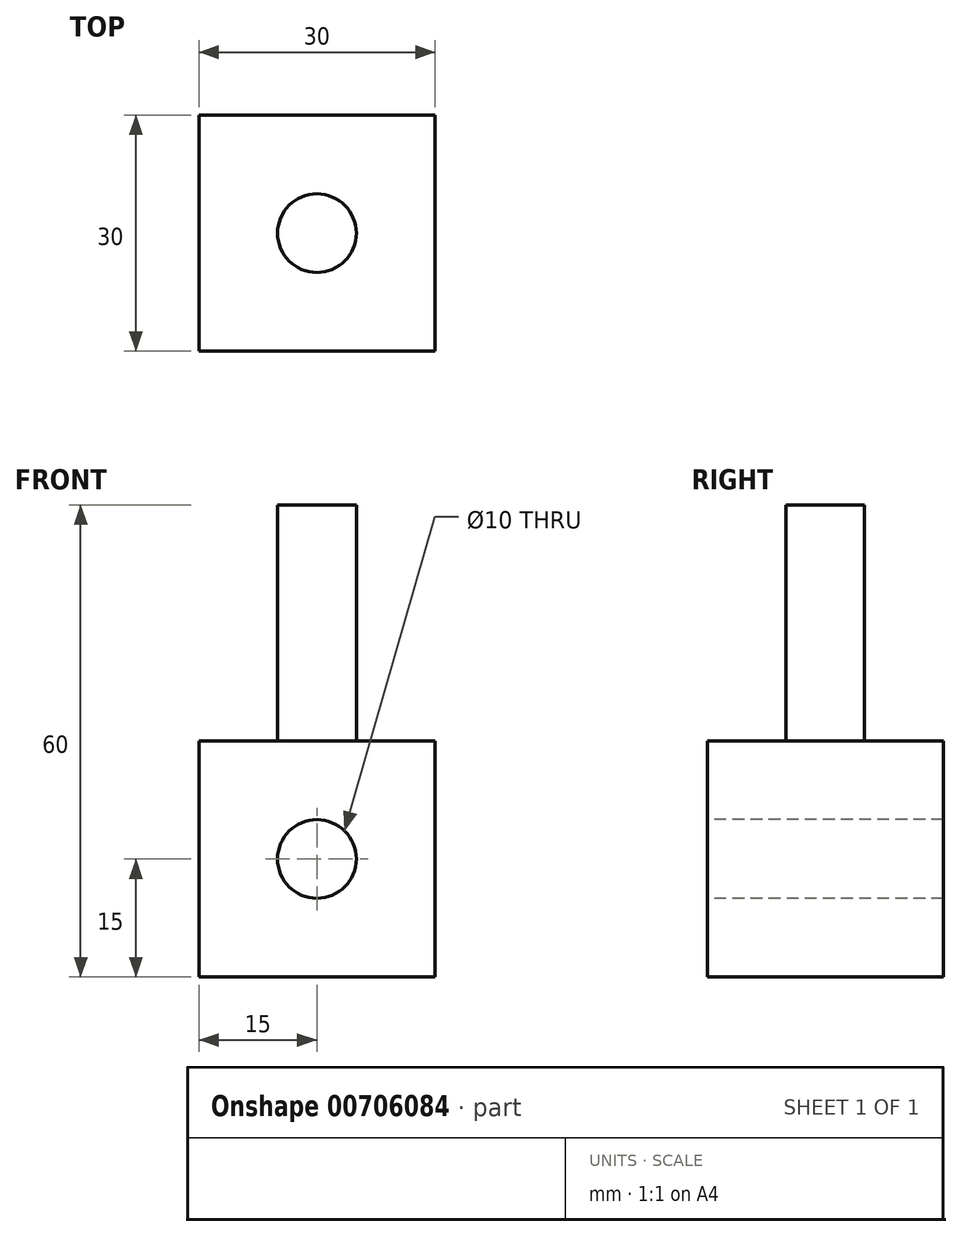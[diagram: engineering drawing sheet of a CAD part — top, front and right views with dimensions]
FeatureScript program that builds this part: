
annotation { "Feature Type Name" : "Feature", "Feature Type Description" : "" }
export const myFeature = defineFeature(function(context is Context, id is Id, definition is map)
    precondition{}
    {
        {
            var Q0;
            Q0=qCreatedBy(makeId("Front.planeOp"),FACE);
            var sketch = newSketch(context, id + "F0", { "sketchPlane" : qUnion([Q0])});
            skLineSegment(sketch, "E0.bottom", {"start": v(15, 15) * mm, "end": v(-15, 15) * mm});
            skLineSegment(sketch, "E0.top", {"start": v(15, -15) * mm, "end": v(-15, -15) * mm});
            skLineSegment(sketch, "E0.left", {"start": v(15, 15) * mm, "end": v(15, -15) * mm});
            skLineSegment(sketch, "E0.right", {"start": v(-15, 15) * mm, "end": v(-15, -15) * mm});
            skPoint(sketch, "E0.middle", {"position": v(0, 0) * mm});
            skSolve(sketch);
        }
        {
            var Q0;
            Q0 = qSketchRegion(id + "F0", true);
            extrude(context, id + "F1", {"entities" : qUnion([Q0]), "depth" : 30 * mm, "offsetDistance" : 25 * mm});
        }
        {
            var Q0;
            Q0=makeQuery(id+"F1.opExtrude","CAP_FACE",FACE,{"disambiguationData":[OSD([sQuery(id+"F0.wireOp",EDGE,"E0.bottom"),sQuery(id+"F0.wireOp",EDGE,"E0.top"),sQuery(id+"F0.wireOp",EDGE,"E0.left"),sQuery(id+"F0.wireOp",EDGE,"E0.right")])],"isStart":false});
            var sketch = newSketch(context, id + "F2", { "sketchPlane" : qUnion([Q0])});
            skCircle(sketch, "E1", {"center": v(0, 0) * mm, "radius": 5 * mm});
            skSolve(sketch);
        }
        {
            var Q0;
            Q0=makeQuery(id+"F2.imprint","IMPRINT",FACE,{"disambiguationData":[TD([[makeQuery(id+"F2.imprint","IMPRINT",EDGE,{"derivedFrom":sQuery(id+"F2.wireOp",EDGE,"E1")}),1.0]])]});
            extrude(context, id + "F3", {"entities" : qUnion([Q0]), "operationType" : NewBodyOperationType.REMOVE, "oppositeDirection" : true, "depth" : 30 * mm, "offsetDistance" : 25 * mm});
        }
        {
            var Q0;
            Q0=makeQuery(id+"F1.opExtrude","SWEPT_FACE",FACE,{"disambiguationData":[OSD([sQuery(id+"F0.wireOp",EDGE,"E0.bottom")])]});
            var sketch = newSketch(context, id + "F4", { "sketchPlane" : qUnion([Q0])});
            skCircle(sketch, "E2", {"center": v(0, -15) * mm, "radius": 5 * mm});
            skPoint(sketch, "E2.centerSnap0", {"position": v(-15, -15) * mm});
            skSolve(sketch);
        }
        {
            var Q0;
            Q0=makeQuery(id+"F4.imprint","IMPRINT",FACE,{"disambiguationData":[TD([[makeQuery(id+"F4.imprint","IMPRINT",EDGE,{"derivedFrom":sQuery(id+"F4.wireOp",EDGE,"E2")}),1.0]])]});
            extrude(context, id + "F5", {"entities" : qUnion([Q0]), "operationType" : NewBodyOperationType.ADD, "depth" : 30 * mm, "offsetDistance" : 25 * mm});
        }
    });
